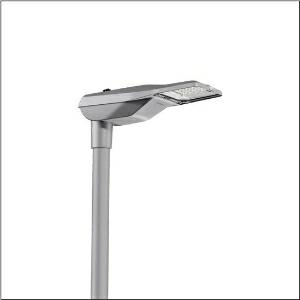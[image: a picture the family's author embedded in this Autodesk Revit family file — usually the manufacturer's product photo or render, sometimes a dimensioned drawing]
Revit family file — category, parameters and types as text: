
# Revit family: streetlight_sl_21_micro___p0_8a_5xe1u33s08db_860c
name_source: partatom
category: Lighting Fixtures
units: mm (PartAtom-declared; Revit-internal decimal feet)

## family parameters
Cut with Voids When Loaded = No
Host = Face
Light Source = No
Part Type = Normal
Room Calculation Point = No
Round Connector Dimension = Use Diameter
Shared = No

## types (1)
- --- (1 x LED, 5040 lm, 39.1 W, 3000K)
    Apparent Load = 39 VA
    CIE Flux Codes = 33 69 96 100 100
    Color Rendering = 70
    Color Temperature = 3000K
    Default Elevation = 1800 mm
    Description = Streetlight SL 21 micro, mast luminaire, primary light control with lens, of PMMA, primary optical cover: cover, of toughened safety glass, transparent, light distribution: P0.8a, light emission: direct distribution, primary light characteristic: asymmetric, installation type: post-top, side-entry, LED, High Power LED, rated luminous flux: 5.040lm, luminous efficacy: 129lm/W, light colour: 730, colour temperature: 3000K, control gear: D4i, control: pre-setting: logarithmic dimming characteristic, flexible luminous flux parameterisation, time-dependent luminous flux control, constant luminous flux control, overheat protection, mains connection: 220..240V, AC, 50/60Hz, start of lifetime: 39W, end of service life: 41W, reduction: 18W, luminaire housing, of diecast aluminium, powder-coated, SITECO metallic grey (DB 702S), corrosivity category C5 high according to DIN EN ISO 12944, multi-level sealing system, sealing non-destructively replaceable, inclination adjustable: 0°, 5°, 10°, 15°, please order mast flange separately, length: 528mm, width: 235mm, height: 110mm, mast flange for spigot size: 42mm (side-entry): 5XC10008XM4, 60/48mm (side-entry/post-top): 5XC10108XM2, 76/60mm (side-entry/post-top): 5XC10108XM1, Smart Interface above, protection rating (complete): IP66, insulation class (complete): insulation class II (safety insulation), certification: CE, ENEC, ENEC+, VDE, impact resistance: IK10, permissible operating ambient temperature for outdoor applications: -40..+50°C, standard-compliant lighting for roads and squares, packaging unit: 1 piece

Light Distribution: P0.8a
    Height = 110 mm
    Lamp = 1 x LED
    Lamp Light Flux = 5040 lm
    Lamp Power = 39.1 W
    Lamp count = 1
    Length = 528 mm
    Luminous efficacy = 129 lm/W
    Manufacturer = Siteco
    ModVariant = No
    Model = 5XE1U33S08DB
    Number of Poles = 1
    OnlyDefault = Yes
    Power Factor = 1
    Product Name = Streetlight SL 21 micro | P0.8a
    Product group = mast luminaire | pylon top
    ProductGroupID = 6100
    Protection Class = Protection class II
    Protection Degree = IP 66
    RLX_Detail_Level = 1
    RLX_Emergency_Light_Flux = 0 lm
    RLX_Emergency_Type = 0
    RLX_Emergency_Type_DB = No
    RlxData = <blob elided: 98573 chars, md5=3a62c5dd>
    Socket = socket
    Standby Power = 0 W
    System Light Flux = 5040 lm
    System Power = 39 W
    Type Comments = factory setting: luminous flux: 100 % | dim-lin: 254 | 765 mA
    Type Image = l_1277292.jpg
    URL = http://relux.com
    VarID = @adj_080555
    Voltage = 0 V
    Weight = 0.00 kg
    Width = 235 mm

## geometry (parser evidence)
native form markers: Blend x4, Sweep x10
no freeform markers — native parametric forms only
